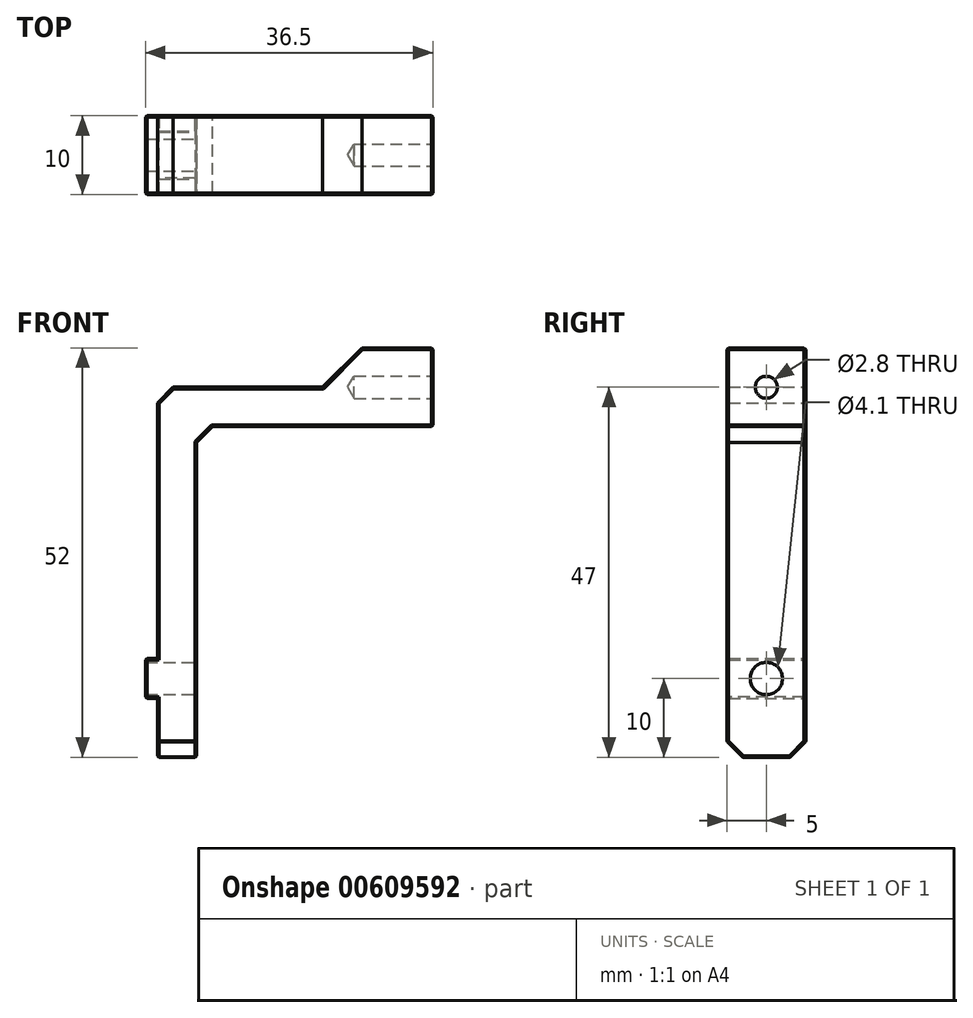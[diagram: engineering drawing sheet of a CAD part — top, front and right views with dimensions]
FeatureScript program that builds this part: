
annotation { "Feature Type Name" : "Feature", "Feature Type Description" : "" }
export const myFeature = defineFeature(function(context is Context, id is Id, definition is map)
    precondition{}
    {
        {
            var Q0;
            Q0=qCreatedBy(makeId("Front.planeOp"),FACE);
            var sketch = newSketch(context, id + "F0", { "sketchPlane" : qUnion([Q0])});
            skLineSegment(sketch, "E0", {"start": v(0, -47) * mm, "end": v(5, -47) * mm});
            skLineSegment(sketch, "E1", {"start": v(5, -47) * mm, "end": v(5, -5) * mm});
            skLineSegment(sketch, "E2", {"start": v(5, -5) * mm, "end": v(35, -5) * mm});
            skLineSegment(sketch, "E3", {"start": v(35, -5) * mm, "end": v(35, 5) * mm});
            skLineSegment(sketch, "E4", {"start": v(35, 5) * mm, "end": v(21, 5) * mm});
            skLineSegment(sketch, "E5", {"start": v(21, 5) * mm, "end": v(21, 0) * mm});
            skLineSegment(sketch, "E6", {"start": v(21, 0) * mm, "end": v(0, 0) * mm});
            skLineSegment(sketch, "E7", {"start": v(0, 0) * mm, "end": v(0, -47) * mm});
            skLineSegment(sketch, "E8", {"start": v(0, -34.45) * mm, "end": v(-1.5, -34.45) * mm});
            skLineSegment(sketch, "E9", {"start": v(-1.5, -34.45) * mm, "end": v(-1.5, -39.55) * mm});
            skLineSegment(sketch, "E10", {"start": v(-1.5, -39.55) * mm, "end": v(0, -39.55) * mm});
            skPoint(sketch, "E11", {"position": v(-1.5, -37) * mm});
            skSolve(sketch);
        }
        {
            var Q0;
            Q0=makeQuery(id+"F0.imprint","IMPRINT",FACE,{"disambiguationData":[TD([[makeQuery(id+"F0.imprint","IMPRINT",EDGE,{"derivedFrom":sQuery(id+"F0.wireOp",EDGE,"E0")}),1.0]])]});
            var Q1;
            {var subQ0=sQuery(id+"F0.wireOp",EDGE,"E8");Q1=makeQuery(id+"F0.imprint","IMPRINT",FACE,{"disambiguationData":[TD([[makeQuery(id+"F0.imprint","IMPRINT",EDGE,{"derivedFrom":subQ0}),1.0]])]});}
            extrude(context, id + "F1", {"entities" : qUnion([Q0, Q1]), "depth" : 10 * mm, "offsetDistance" : 25 * mm});
        }
        {
            var Q0;
            Q0=makeQuery(id+"F1.opExtrude","SWEPT_EDGE",EDGE,{"disambiguationData":[OSD([sQuery(id+"F0.wireOp",EDGE,"E6"),sQuery(id+"F0.wireOp",EDGE,"E7")])]});
            var Q1;
            Q1=makeQuery(id+"F1.opExtrude","SWEPT_EDGE",EDGE,{"disambiguationData":[OSD([sQuery(id+"F0.wireOp",EDGE,"E1"),sQuery(id+"F0.wireOp",EDGE,"E2")])]});
            var Q2;
            Q2=makeQuery(id+"F1.opExtrude","CAP_EDGE",EDGE,{"disambiguationData":[OSD([sQuery(id+"F0.wireOp",EDGE,"E0")])],"isStart":false});
            var Q3;
            Q3=makeQuery(id+"F1.opExtrude","CAP_EDGE",EDGE,{"disambiguationData":[OSD([sQuery(id+"F0.wireOp",EDGE,"E0")])],"isStart":true});
            chamfer(context, id + "F2", {"entities" : qUnion([Q0, Q1, Q2, Q3]), "width" : 2 * mm, "tangentPropagation" : true});
        }
        {
            var Q0;
            Q0=makeQuery(id+"F1.opExtrude","SWEPT_EDGE",EDGE,{"disambiguationData":[OSD([sQuery(id+"F0.wireOp",EDGE,"E4"),sQuery(id+"F0.wireOp",EDGE,"E5")])]});
            chamfer(context, id + "F3", {"entities" : qUnion([Q0]), "width" : 5 * mm, "tangentPropagation" : true});
        }
        {
            var Q0;
            Q0=makeQuery(id+"F1.opExtrude","SWEPT_FACE",FACE,{"disambiguationData":[OSD([sQuery(id+"F0.wireOp",EDGE,"E3")])]});
            var sketch = newSketch(context, id + "F4", { "sketchPlane" : qUnion([Q0])});
            skPoint(sketch, "E12", {"position": v(-5, 0) * mm});
            skSolve(sketch);
        }
        {
            var Q0;
            Q0=makeQuery(id+"F1.opExtrude","SWEPT_FACE",FACE,{"disambiguationData":[OSD([sQuery(id+"F0.wireOp",EDGE,"E1")])]});
            var sketch = newSketch(context, id + "F5", { "sketchPlane" : qUnion([Q0])});
            skPoint(sketch, "E13", {"position": v(-5, -37) * mm});
            skSolve(sketch);
        }
        {
            var Q0;
            Q0=sQuery(id+"F4.wireOp",VERTEX,"E12");
            var Q1;
            Q1=makeQuery(id+"F1.opExtrude","SWEPT_BODY",BODY,{"disambiguationData":[OSD([sQuery(id+"F0.wireOp",EDGE,"E0"),sQuery(id+"F0.wireOp",EDGE,"E1"),sQuery(id+"F0.wireOp",EDGE,"E2"),sQuery(id+"F0.wireOp",EDGE,"E3"),sQuery(id+"F0.wireOp",EDGE,"E4"),sQuery(id+"F0.wireOp",EDGE,"E5"),sQuery(id+"F0.wireOp",EDGE,"E6"),sQuery(id+"F0.wireOp",EDGE,"E7")])]});
            hole(context, id + "F6", {"style" : HoleStyle.SIMPLE, "endStyle" : HoleEndStyle.BLIND, "holeDiameter" : 2.8 * mm, "majorDiameter" : 5 * mm, "holeDepth" : 10 * mm, "isTappedThrough" : true, "tappedDepth" : 12 * mm, "tapClearance" : 3, "locations" : qUnion([Q0]), "scope" : qUnion([Q1])});
        }
        {
            var Q0;
            Q0=sQuery(id+"F5.wireOp",VERTEX,"E13");
            var Q1;
            Q1=makeQuery(id+"F1.opExtrude","SWEPT_BODY",BODY,{"disambiguationData":[OSD([sQuery(id+"F0.wireOp",EDGE,"E0"),sQuery(id+"F0.wireOp",EDGE,"E1"),sQuery(id+"F0.wireOp",EDGE,"E2"),sQuery(id+"F0.wireOp",EDGE,"E3"),sQuery(id+"F0.wireOp",EDGE,"E4"),sQuery(id+"F0.wireOp",EDGE,"E5"),sQuery(id+"F0.wireOp",EDGE,"E6"),sQuery(id+"F0.wireOp",EDGE,"E7")])]});
            hole(context, id + "F7", {"style" : HoleStyle.SIMPLE, "endStyle" : HoleEndStyle.THROUGH, "holeDiameter" : 4.1 * mm, "majorDiameter" : 5 * mm, "isTappedThrough" : true, "tappedDepth" : 12 * mm, "tapClearance" : 3, "locations" : qUnion([Q0]), "scope" : qUnion([Q1])});
        }
        {
            var Q0;
            Q0=makeQuery(id+"F1.opExtrude","CAP_FACE",FACE,{"disambiguationData":[OSD([sQuery(id+"F0.wireOp",EDGE,"E0"),sQuery(id+"F0.wireOp",EDGE,"E1"),sQuery(id+"F0.wireOp",EDGE,"E2"),sQuery(id+"F0.wireOp",EDGE,"E3"),sQuery(id+"F0.wireOp",EDGE,"E4"),sQuery(id+"F0.wireOp",EDGE,"E5"),sQuery(id+"F0.wireOp",EDGE,"E6"),sQuery(id+"F0.wireOp",EDGE,"E7")])],"isStart":false});
            var Q1;
            Q1=makeQuery(id+"F1.opExtrude","CAP_FACE",FACE,{"disambiguationData":[OSD([sQuery(id+"F0.wireOp",EDGE,"E0"),sQuery(id+"F0.wireOp",EDGE,"E1"),sQuery(id+"F0.wireOp",EDGE,"E2"),sQuery(id+"F0.wireOp",EDGE,"E3"),sQuery(id+"F0.wireOp",EDGE,"E4"),sQuery(id+"F0.wireOp",EDGE,"E5"),sQuery(id+"F0.wireOp",EDGE,"E6"),sQuery(id+"F0.wireOp",EDGE,"E7")])],"isStart":true});
            var Q2;
            Q2=makeQuery(id+"F1.opExtrude","SWEPT_EDGE",EDGE,{"disambiguationData":[OSD([sQuery(id+"F0.wireOp",EDGE,"E3"),sQuery(id+"F0.wireOp",EDGE,"E4")])]});
            var Q3;
            Q3=makeQuery(id+"F1.opExtrude","SWEPT_EDGE",EDGE,{"disambiguationData":[OSD([sQuery(id+"F0.wireOp",EDGE,"E2"),sQuery(id+"F0.wireOp",EDGE,"E3")])]});
            var Q4;
            Q4=makeQuery(id+"F1.opExtrude","SWEPT_FACE",FACE,{"disambiguationData":[OSD([sQuery(id+"F0.wireOp",EDGE,"E0")])]});
            var Q5;
            {var subQ0=sQuery(id+"F0.wireOp",EDGE,"E0");Q5=makeQuery(id+"F2.opChamfer","BLEND_FACE",FACE,{"disambiguationData":[OSD([subQ0]),TDD([makeQuery(id+"F1.opExtrude","CAP_EDGE",EDGE,{"disambiguationData":[OSD([subQ0])],"isStart":false})])]});}
            var Q6;
            {var subQ0=sQuery(id+"F0.wireOp",EDGE,"E0");Q6=makeQuery(id+"F2.opChamfer","BLEND_FACE",FACE,{"disambiguationData":[OSD([subQ0]),TDD([makeQuery(id+"F1.opExtrude","CAP_EDGE",EDGE,{"disambiguationData":[OSD([subQ0])],"isStart":true})])]});}
            var Q7;
            Q7=makeQuery(id+"F1.opExtrude","SWEPT_EDGE",EDGE,{"disambiguationData":[OSD([sQuery(id+"F0.wireOp",EDGE,"E8"),sQuery(id+"F0.wireOp",EDGE,"E9")])]});
            var Q8;
            Q8=makeQuery(id+"F1.opExtrude","SWEPT_EDGE",EDGE,{"disambiguationData":[OSD([sQuery(id+"F0.wireOp",EDGE,"E9"),sQuery(id+"F0.wireOp",EDGE,"E10")])]});
            chamfer(context, id + "F8", {"entities" : qUnion([Q0, Q1, Q2, Q3, Q4, Q5, Q6, Q7, Q8]), "width" : 0.2 * mm, "tangentPropagation" : true});
        }
    });
